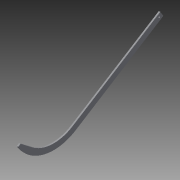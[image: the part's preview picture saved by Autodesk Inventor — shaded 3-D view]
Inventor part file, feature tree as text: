
AUTODESK INVENTOR PART (.ipt)
format: ipt  version: 2013 (Build 170138000, 138)  size: 107,520 bytes
history: native  units: in
note: dims shown in document units (in); Inventor stores cm internally (conversion verified against a paired STEP export)
features: extrude x2, sketch x2
ambient origin geometry x8: Origin, YZ Plane, XZ Plane, XY Plane, X Axis, Y Axis, Z Axis, Center Point
bodies: Solid1 (feature_tree)
feature tree (4):
  extrude  "Extrusion1"  Depth=10.39in
  extrude  "Extrusion2"  Depth=1.0in
  sketch  "Sketch1"  dims[d5=12.0in d6=10.39in]
  sketch  "Sketch2"  dims[d7=1.0in d8=1.0in d9=20.0in d10=3.0in d11=5.0in d12=0.5in d13=1.0in d14=1.0in d15=12.0in d16=1.0in d17=0.5in d18=0.25in d19=0.0in d20=0.5in d21=0.25in d22=1.0in d23=0.0in]
